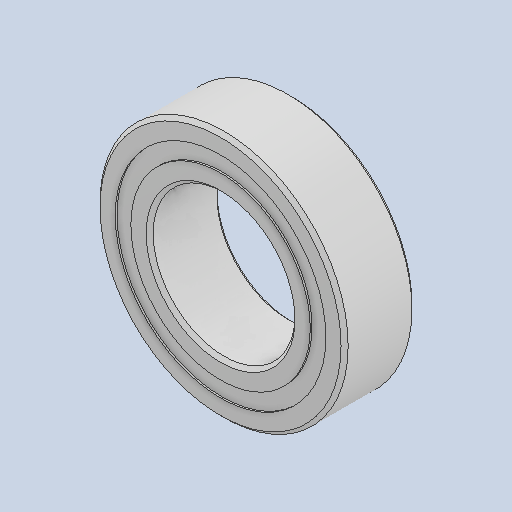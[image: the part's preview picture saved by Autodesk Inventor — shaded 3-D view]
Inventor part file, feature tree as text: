
AUTODESK INVENTOR PART (.ipt)
format: ipt  version: 2024.2 (Build 282272000, 272)  size: 586,752 bytes
history: native  units: in
note: dims shown in document units (in); Inventor stores cm internally (conversion verified against a paired STEP export)
features: other x11, revolve x5
ambient origin geometry x8: Origin, YZ Plane, XZ Plane, XY Plane, X Axis, Y Axis, Z Axis, Center Point
bodies: Solid1 (feature_tree), Solid2 (feature_tree), Solid3 (feature_tree), Solid4 (feature_tree), Solid5 (feature_tree), Solid6 (feature_tree), Solid7 (feature_tree), Solid8 (feature_tree), Solid9 (feature_tree), Solid10 (feature_tree), Solid11 (feature_tree), Solid12 (feature_tree), Solid13 (feature_tree), Solid14 (feature_tree), Solid15 (feature_tree), Solid16 (feature_tree)
feature tree (16):
  revolve  "Revolve1"  [1 undecoded]
  revolve  "Revolve3"  [1 undecoded]
  revolve  "Revolve4"  [1 undecoded]
  other  "CirPattern1[1]"
  other  "CirPattern1[2]"
  other  "CirPattern1[3]"
  other  "CirPattern1[4]"
  other  "CirPattern1[5]"
  other  "CirPattern1[6]"
  other  "CirPattern1[7]"
  other  "CirPattern1[8]"
  other  "CirPattern1[9]"
  other  "CirPattern1[10]"
  other  "CirPattern1[11]"
  revolve  "Revolve5[1]"  [1 undecoded]
  revolve  "Revolve5[2]"  [1 undecoded]
note: 5 required parameter values undecoded (feature->parameter linkage not recoverable at this tier; creation-order binding heuristic only, values carry confidence <= 0.55)
